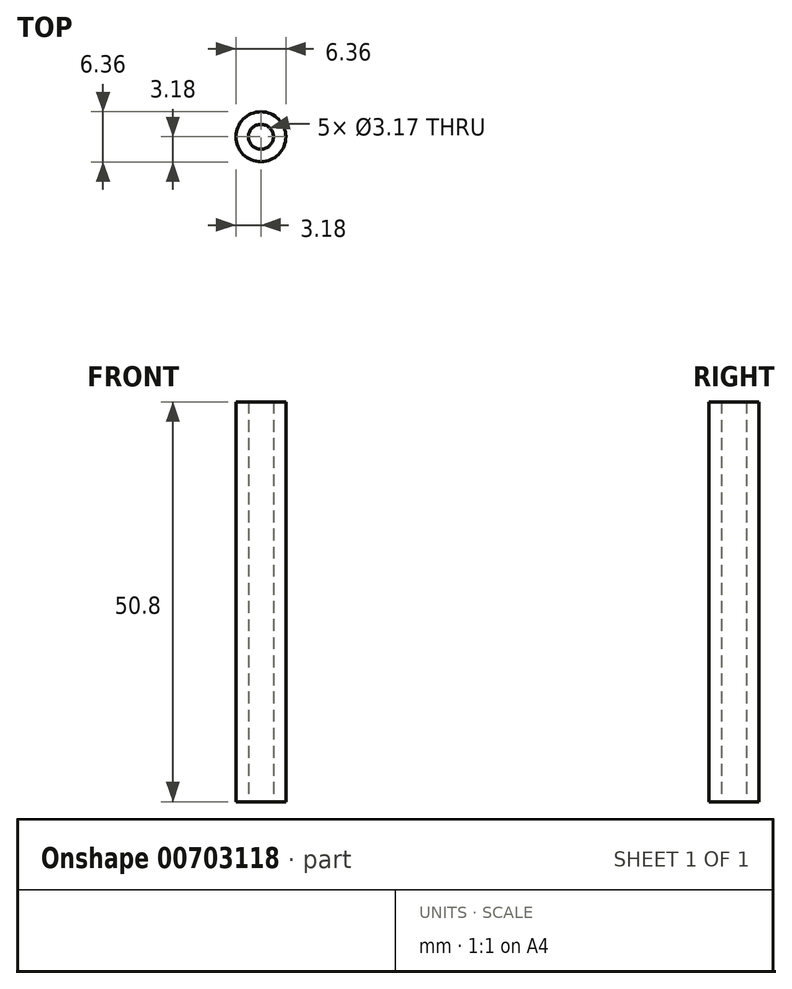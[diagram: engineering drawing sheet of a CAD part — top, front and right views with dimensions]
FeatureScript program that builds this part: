
annotation { "Feature Type Name" : "Feature", "Feature Type Description" : "" }
export const myFeature = defineFeature(function(context is Context, id is Id, definition is map)
    precondition{}
    {
        {
            var Q0;
            Q0=qCreatedBy(makeId("Front.planeOp"),FACE);
            var sketch = newSketch(context, id + "F0", { "sketchPlane" : qUnion([Q0])});
            skLineSegment(sketch, "E0.bottom", {"start": v(1.59, 50.8) * mm, "end": v(3.17, 50.8) * mm});
            skLineSegment(sketch, "E0.top", {"start": v(1.59, 0) * mm, "end": v(3.18, 0) * mm});
            skLineSegment(sketch, "E0.left", {"start": v(3.17, 50.8) * mm, "end": v(3.18, 0) * mm});
            skLineSegment(sketch, "E0.right", {"start": v(1.59, 50.8) * mm, "end": v(1.59, 0) * mm});
            skSolve(sketch);
        }
        {
            var Q0;
            Q0=qCreatedBy(makeId("Front.planeOp"),FACE);
            var sketch = newSketch(context, id + "F1", { "sketchPlane" : qUnion([Q0])});
            skLineSegment(sketch, "E1", {"start": v(0, 0) * mm, "end": v(0, 35.94) * mm});
            skSolve(sketch);
        }
        {
            var Q0;
            Q0=makeQuery(id+"F0.imprint","IMPRINT",FACE,{"disambiguationData":[TD([[makeQuery(id+"F0.imprint","IMPRINT",EDGE,{"derivedFrom":sQuery(id+"F0.wireOp",EDGE,"E0.bottom")}),-1.0]])]});
            var Q1;
            Q1=sQuery(id+"F1.wireOp",EDGE,"E1");
            revolve(context, id + "F2", {"surfaceOperationType" : NewSurfaceOperationType.NEW, "entities" : qUnion([Q0]), "axis" : qUnion([Q1]), "revolveType" : RevolveType.FULL});
        }
    });
